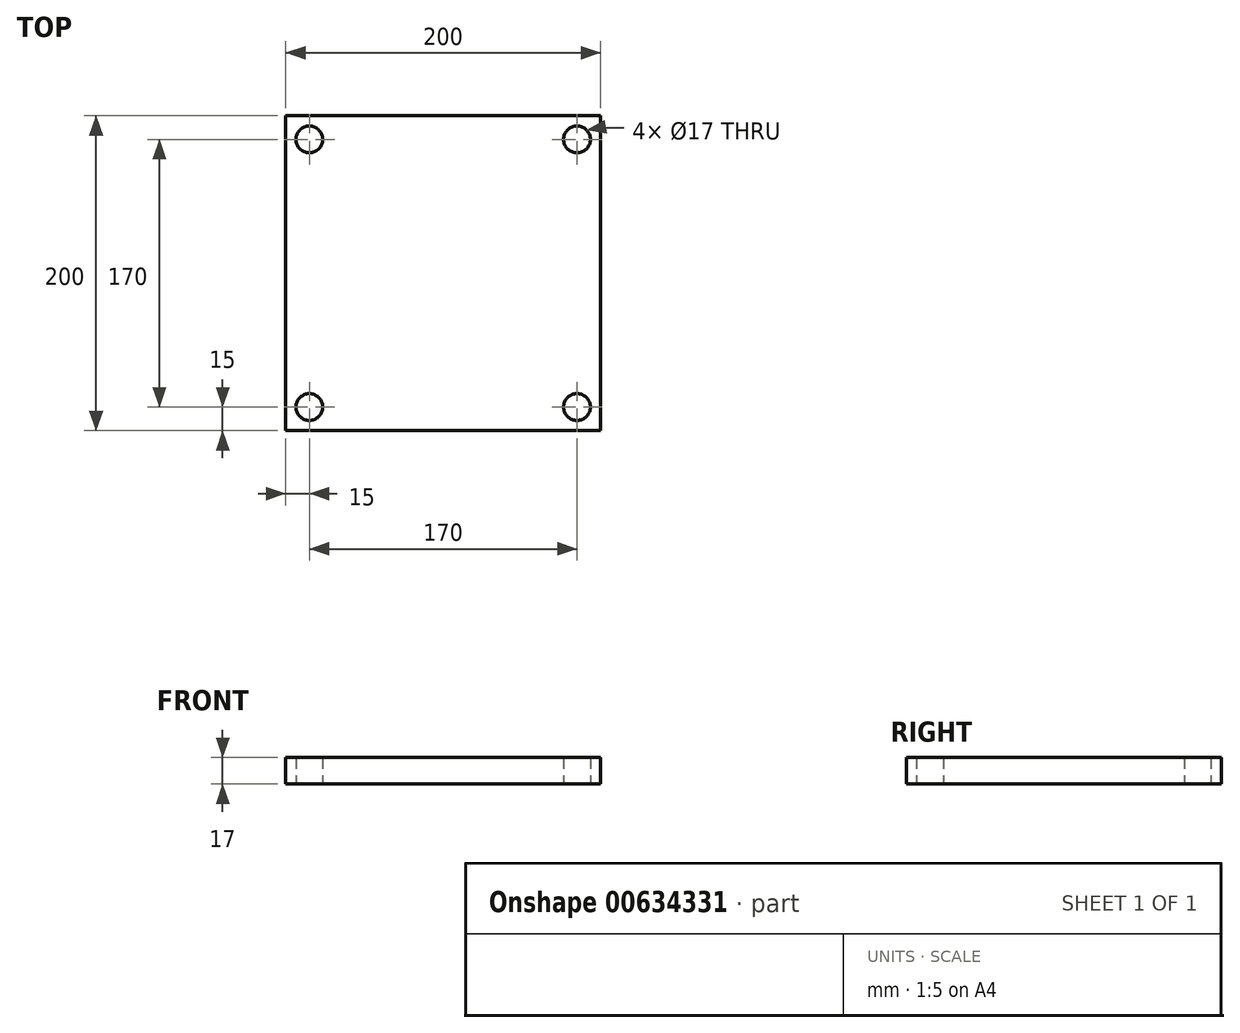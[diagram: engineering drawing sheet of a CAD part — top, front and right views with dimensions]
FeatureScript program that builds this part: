
annotation { "Feature Type Name" : "Feature", "Feature Type Description" : "" }
export const myFeature = defineFeature(function(context is Context, id is Id, definition is map)
    precondition{}
    {
        {
            var Q0;
            Q0=qCreatedBy(makeId("Top.planeOp"),FACE);
            var sketch = newSketch(context, id + "F0", { "sketchPlane" : qUnion([Q0])});
            skLineSegment(sketch, "E0.bottom", {"start": v(100, 100) * mm, "end": v(-100, 100) * mm});
            skLineSegment(sketch, "E0.top", {"start": v(100, -100) * mm, "end": v(-100, -100) * mm});
            skLineSegment(sketch, "E0.left", {"start": v(100, 100) * mm, "end": v(100, -100) * mm});
            skLineSegment(sketch, "E0.right", {"start": v(-100, 100) * mm, "end": v(-100, -100) * mm});
            skPoint(sketch, "E0.middle", {"position": v(0, 0) * mm});
            skCircle(sketch, "E1", {"center": v(85, 85) * mm, "radius": 8.5 * mm});
            skCircle(sketch, "E2", {"center": v(85, -85) * mm, "radius": 8.5 * mm});
            skCircle(sketch, "E3", {"center": v(-85, -85) * mm, "radius": 8.5 * mm});
            skCircle(sketch, "E4", {"center": v(-85, 85) * mm, "radius": 8.5 * mm});
            skSolve(sketch);
        }
        {
            var Q0;
            Q0 = qSketchRegion(id + "F0", true);
            extrude(context, id + "F1", {"entities" : qUnion([Q0]), "depth" : 20 * mm, "offsetDistance" : 25 * mm});
        }
        {
            var Q0;
            Q0=makeQuery(id+"F1.opExtrude","CAP_FACE",FACE,{"disambiguationData":[OSD([sQuery(id+"F0.wireOp",EDGE,"E0.bottom"),sQuery(id+"F0.wireOp",EDGE,"E0.top"),sQuery(id+"F0.wireOp",EDGE,"E0.left"),sQuery(id+"F0.wireOp",EDGE,"E0.right")])],"isStart":true});
            var sketch = newSketch(context, id + "F2", { "sketchPlane" : qUnion([Q0])});
            skLineSegment(sketch, "E5.bottom", {"start": v(132.88, 117.5) * mm, "end": v(-132.88, 117.5) * mm});
            skLineSegment(sketch, "E5.top", {"start": v(132.88, -117.5) * mm, "end": v(-132.88, -117.5) * mm});
            skLineSegment(sketch, "E5.left", {"start": v(132.88, 117.5) * mm, "end": v(132.88, -117.5) * mm});
            skLineSegment(sketch, "E5.right", {"start": v(-132.88, 117.5) * mm, "end": v(-132.88, -117.5) * mm});
            skPoint(sketch, "E5.middle", {"position": v(0, 0) * mm});
            skSolve(sketch);
        }
        {
            var Q0;
            Q0 = qSketchRegion(id + "F2", true);
            extrude(context, id + "F3", {"entities" : qUnion([Q0]), "operationType" : NewBodyOperationType.REMOVE, "oppositeDirection" : true, "depth" : 3 * mm, "offsetDistance" : 25 * mm});
        }
    });
